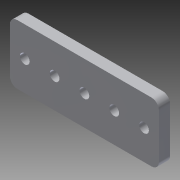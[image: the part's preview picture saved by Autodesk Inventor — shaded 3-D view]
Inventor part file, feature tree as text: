
AUTODESK INVENTOR PART (.ipt)
format: ipt  version: 2014 SP1 (Build 180222100, 222)  size: 107,520 bytes
history: native  units: in
note: dims shown in document units (in); Inventor stores cm internally (conversion verified against a paired STEP export)
features: extrude x1, fillet x1, sketch x1
ambient origin geometry x8: Origin, YZ Plane, XZ Plane, XY Plane, X Axis, Y Axis, Z Axis, Center Point
bodies: Solid1 (feature_tree)
feature tree (3):
  extrude  "Extrusion1"  TaperAngle=90.0deg  [1 undecoded]
  fillet  "Fillet1"  Radius=2.5in
  sketch  "Sketch1"  dims[d0=0.163in d1=90.0deg d2=2.5in d3=0.0in d4=1.0in d5=2.415in d6=0.0in d7=0.085in d8=0.085in d9=0.25in d10=0.5in d11=0.75in d12=0.5in d13=1.25in d14=0.5in d15=1.75in d16=0.5in d17=2.25in d18=0.5in d19=2.415in d20=0.085in d21=1.0in d22=0.1875in d23=0.0in d24=0.125in]
note: 1 required parameter value undecoded (feature->parameter linkage not recoverable at this tier; creation-order binding heuristic only, values carry confidence <= 0.55)
